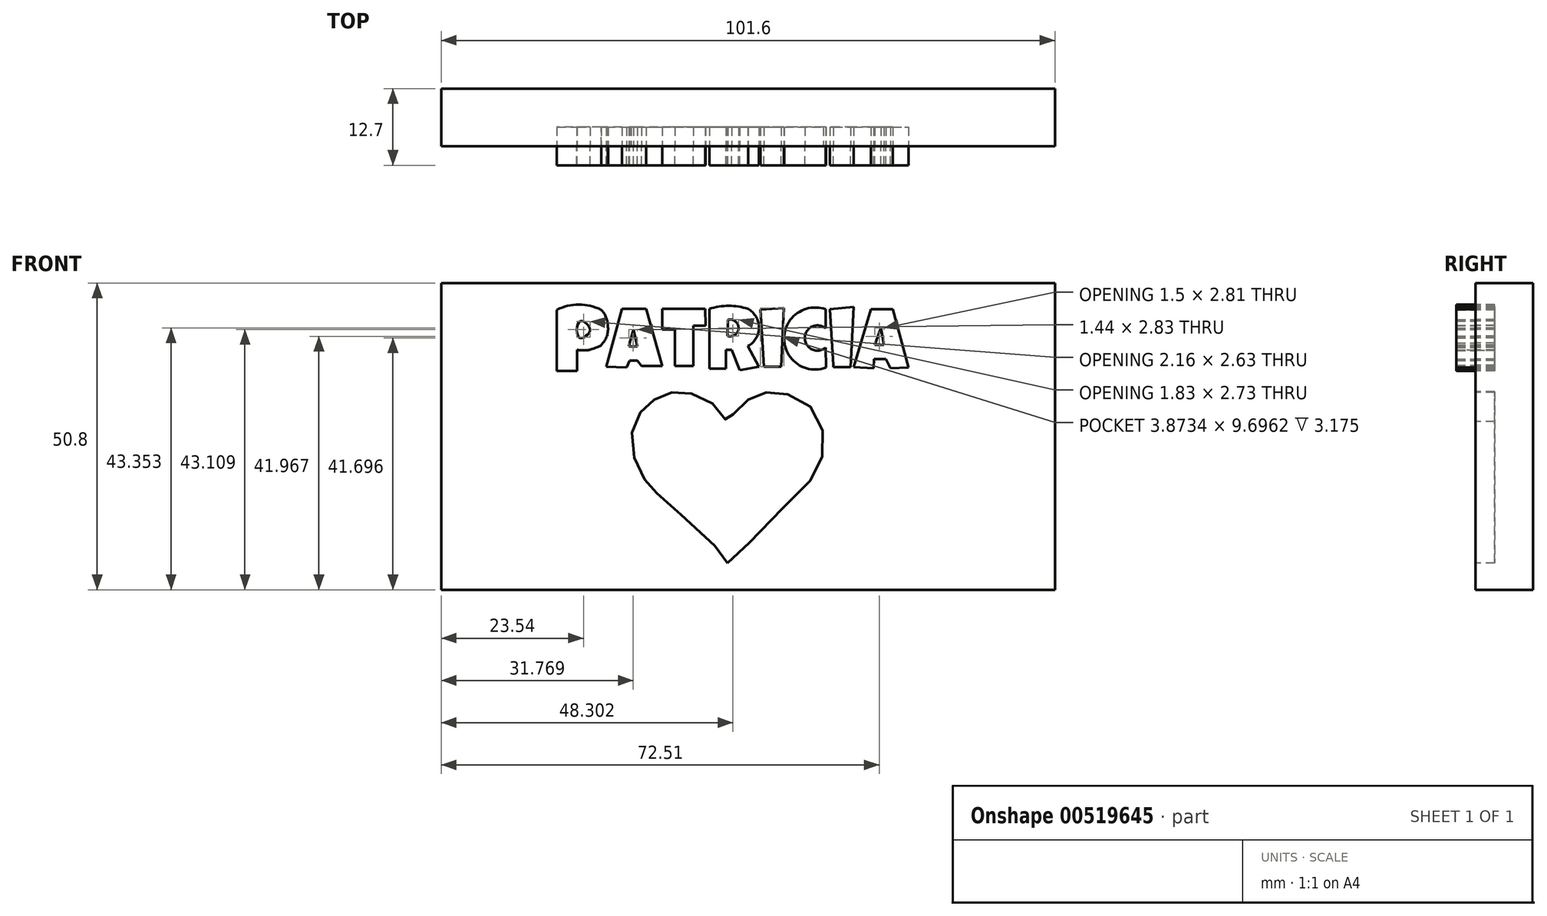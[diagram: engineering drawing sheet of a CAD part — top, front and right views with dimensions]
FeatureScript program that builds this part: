
annotation { "Feature Type Name" : "Feature", "Feature Type Description" : "" }
export const myFeature = defineFeature(function(context is Context, id is Id, definition is map)
    precondition{}
    {
        {
            var Q0;
            Q0=qCreatedBy(makeId("Front.planeOp"),FACE);
            var Q1;
            Q1=qCreatedBy(makeId("Front.planeOp"),FACE);
            var Q2;
            Q2=qCreatedBy(makeId("Front.planeOp"),FACE);
            var Q3;
            Q3=qCreatedBy(makeId("Front.planeOp"),FACE);
            var sketch = newSketch(context, id + "F0", { "sketchPlane" : qUnion([Q0, Q1, Q2, Q3])});
            skLineSegment(sketch, "E0.bottom", {"start": v(-89.5, 39.79) * mm, "end": v(12.1, 39.79) * mm});
            skLineSegment(sketch, "E0.top", {"start": v(-89.5, -11.01) * mm, "end": v(12.1, -11.01) * mm});
            skLineSegment(sketch, "E0.left", {"start": v(-89.5, 39.79) * mm, "end": v(-89.5, -11.01) * mm});
            skLineSegment(sketch, "E0.right", {"start": v(12.1, 39.79) * mm, "end": v(12.1, -11.01) * mm});
            skSolve(sketch);
        }
        {
            var Q0;
            Q0=makeQuery(id+"F0.imprint","IMPRINT",FACE,{"disambiguationData":[TD([[makeQuery(id+"F0.imprint","IMPRINT",EDGE,{"derivedFrom":sQuery(id+"F0.wireOp",EDGE,"E0.bottom")}),-1.0]])]});
            extrude(context, id + "F1", {"entities" : qUnion([Q0]), "depth" : 9.52 * mm, "offsetDistance" : 25.4 * mm});
        }
        {
            var Q0;
            Q0=makeQuery(id+"F1.opExtrude","CAP_FACE",FACE,{"disambiguationData":[OSD([sQuery(id+"F0.wireOp",EDGE,"E0.bottom"),sQuery(id+"F0.wireOp",EDGE,"E0.top"),sQuery(id+"F0.wireOp",EDGE,"E0.left"),sQuery(id+"F0.wireOp",EDGE,"E0.right")])],"isStart":false});
            var sketch = newSketch(context, id + "F2", { "sketchPlane" : qUnion([Q0])});
            skLineSegment(sketch, "E1", {"start": v(-70.4, 35.35) * mm, "end": v(-70.4, 25.24) * mm});
            skLineSegment(sketch, "E2", {"start": v(-70.4, 25.24) * mm, "end": v(-66.98, 25.24) * mm});
            skLineSegment(sketch, "E3", {"start": v(-66.98, 25.24) * mm, "end": v(-66.98, 28.77) * mm});
            skArc(sketch, "E4", {"start": v(-63.03, 35.35) * mm, "mid": v(-66.71, 36.2) * mm, "end": v(-70.4, 35.35) * mm});
            skArc(sketch, "E5", {"start": v(-61.93, 32.72) * mm, "mid": v(-62.22, 34.15) * mm, "end": v(-63.03, 35.35) * mm});
            skArc(sketch, "E6", {"start": v(-63.03, 29.54) * mm, "mid": v(-62.08, 31) * mm, "end": v(-61.93, 32.72) * mm});
            skFitSpline(sketch, "E7", {"points": [v(-63.03, 29.54) * mm, v(-64.56, 28.84) * mm, v(-65.66, 28.64) * mm, v(-66.98, 28.77) * mm, v(-63.03, 29.54) * mm]});
            skFitSpline(sketch, "E8", {"points": [v(-58.8, 25.8) * mm, v(-58.32, 26.97) * mm], "startDerivative": vector(0.48, 1.18) * mm, "endDerivative": vector(0.48, 1.18) * mm});
            skFitSpline(sketch, "E9", {"points": [v(-58.32, 26.97) * mm, v(-57, 26.97) * mm], "startDerivative": vector(1.32, 0) * mm, "endDerivative": vector(1.32, 0) * mm});
            skLineSegment(sketch, "E10", {"start": v(-59.57, 35.5) * mm, "end": v(-62.2, 25.93) * mm});
            skLineSegment(sketch, "E11", {"start": v(-62.2, 25.93) * mm, "end": v(-58.8, 25.8) * mm});
            skLineSegment(sketch, "E12", {"start": v(-57.89, 26.97) * mm, "end": v(-57, 26.97) * mm});
            skLineSegment(sketch, "E13", {"start": v(-59.57, 35.5) * mm, "end": v(-55.55, 35.5) * mm});
            skLineSegment(sketch, "E14", {"start": v(-55.55, 35.5) * mm, "end": v(-52.92, 26.06) * mm});
            skLineSegment(sketch, "E15", {"start": v(-57.7, 32.1) * mm, "end": v(-58.32, 29.83) * mm});
            skLineSegment(sketch, "E16", {"start": v(-57, 29.27) * mm, "end": v(-57.7, 32.1) * mm});
            skLineSegment(sketch, "E17", {"start": v(-52.92, 35.5) * mm, "end": v(-52.92, 32.1) * mm});
            skLineSegment(sketch, "E18", {"start": v(-52.92, 32.1) * mm, "end": v(-50.84, 32.1) * mm});
            skLineSegment(sketch, "E19", {"start": v(-50.84, 32.1) * mm, "end": v(-50.84, 26.06) * mm});
            skLineSegment(sketch, "E20", {"start": v(-50.84, 26.06) * mm, "end": v(-47.8, 26.06) * mm});
            skLineSegment(sketch, "E21", {"start": v(-47.8, 26.06) * mm, "end": v(-47.8, 32.72) * mm});
            skLineSegment(sketch, "E22", {"start": v(-45.1, 32.25) * mm, "end": v(-45.1, 35.5) * mm});
            skPoint(sketch, "E23.end.orphan", {"position": v(-56.31, 26.06) * mm});
            skLineSegment(sketch, "E24", {"start": v(-47.8, 32.72) * mm, "end": v(-45.74, 32.72) * mm});
            skLineSegment(sketch, "E25", {"start": v(-45.1, 32.72) * mm, "end": v(-45.1, 32.72) * mm});
            skLineSegment(sketch, "E26", {"start": v(-45.1, 25.59) * mm, "end": v(-42.4, 25.59) * mm});
            skLineSegment(sketch, "E27", {"start": v(-42.4, 25.59) * mm, "end": v(-42.4, 28.7) * mm});
            skLineSegment(sketch, "E28", {"start": v(-42.4, 28.7) * mm, "end": v(-41.43, 28.7) * mm});
            skLineSegment(sketch, "E29", {"start": v(-41.43, 28.7) * mm, "end": v(-40.1, 25.38) * mm});
            skLineSegment(sketch, "E30", {"start": v(-40.1, 25.38) * mm, "end": v(-36.92, 25.93) * mm});
            skLineSegment(sketch, "E31", {"start": v(-36.92, 25.93) * mm, "end": v(-38.72, 29.33) * mm});
            skLineSegment(sketch, "E32", {"start": v(-36.65, 35.5) * mm, "end": v(-36.1, 25.93) * mm});
            skLineSegment(sketch, "E33", {"start": v(-36.1, 25.93) * mm, "end": v(-33.25, 25.93) * mm});
            skLineSegment(sketch, "E34", {"start": v(-33.25, 25.93) * mm, "end": v(-32.77, 35.63) * mm});
            skLineSegment(sketch, "E35", {"start": v(-32.77, 35.63) * mm, "end": v(-36.64, 35.4) * mm});
            skLineSegment(sketch, "E36", {"start": v(-25.84, 35.42) * mm, "end": v(-25.84, 32.25) * mm});
            skLineSegment(sketch, "E37", {"start": v(-25.15, 35.42) * mm, "end": v(-24.6, 26.21) * mm});
            skLineSegment(sketch, "E38", {"start": v(-24.6, 26.21) * mm, "end": v(-24.6, 25.86) * mm});
            skLineSegment(sketch, "E39", {"start": v(-24.6, 25.86) * mm, "end": v(-21.76, 25.86) * mm});
            skLineSegment(sketch, "E40", {"start": v(-21.76, 25.86) * mm, "end": v(-21.2, 35.84) * mm});
            skLineSegment(sketch, "E41", {"start": v(-21.2, 35.84) * mm, "end": v(-25.15, 35.42) * mm});
            skLineSegment(sketch, "E42", {"start": v(-21.25, 25.84) * mm, "end": v(-17.92, 25.65) * mm});
            skLineSegment(sketch, "E43", {"start": v(-17.92, 25.65) * mm, "end": v(-17.84, 27.2) * mm});
            skLineSegment(sketch, "E44", {"start": v(-17.84, 27.2) * mm, "end": v(-15.87, 27.2) * mm});
            skLineSegment(sketch, "E45", {"start": v(-15.87, 27.2) * mm, "end": v(-15.1, 25.65) * mm});
            skLineSegment(sketch, "E46", {"start": v(-15.1, 25.65) * mm, "end": v(-12.16, 25.83) * mm});
            skLineSegment(sketch, "E47", {"start": v(-14.76, 35.42) * mm, "end": v(-18.36, 35.42) * mm});
            skPoint(sketch, "E48.end.orphan", {"position": v(-25.84, 26.21) * mm});
            skPoint(sketch, "E48.start.orphan", {"position": v(-25.84, 29.12) * mm});
            skLineSegment(sketch, "E49", {"start": v(-25.8, 25.78) * mm, "end": v(-25.84, 29.12) * mm});
            skPoint(sketch, "E50.0.internal.snap0", {"position": v(-66.71, 36.2) * mm});
            skPoint(sketch, "E50.1.internal.snap0", {"position": v(-66.71, 36.2) * mm});
            skFitSpline(sketch, "E50", {"points": [v(-66.71, 33.3) * mm, v(-66.71, 30.8) * mm, v(-65.31, 31.22) * mm, v(-64.89, 32.17) * mm, v(-65.66, 33.24) * mm, v(-66.71, 33.3) * mm]});
            skArc(sketch, "E51", {"start": v(-25.84, 32.25) * mm, "mid": v(-29.3, 30.68) * mm, "end": v(-25.84, 29.12) * mm});
            skArc(sketch, "E52", {"start": v(-25.84, 35.42) * mm, "mid": v(-32.75, 30.57) * mm, "end": v(-25.8, 25.78) * mm});
            skArc(sketch, "E53", {"start": v(-42.11, 31.04) * mm, "mid": v(-40.28, 32.3) * mm, "end": v(-42.03, 33.69) * mm});
            skLineSegment(sketch, "E54", {"start": v(-42.03, 33.69) * mm, "end": v(-42.11, 31.04) * mm});
            skArc(sketch, "E55", {"start": v(-38.71, 35.5) * mm, "mid": v(-41.9, 36) * mm, "end": v(-45.1, 35.5) * mm});
            skArc(sketch, "E56", {"start": v(-38.72, 29.33) * mm, "mid": v(-36.9, 32.4) * mm, "end": v(-38.71, 35.5) * mm});
            skLineSegment(sketch, "E57", {"start": v(-16.74, 32.36) * mm, "end": v(-17.74, 29.55) * mm});
            skLineSegment(sketch, "E58", {"start": v(-17.74, 29.55) * mm, "end": v(-16.24, 29.55) * mm});
            skLineSegment(sketch, "E59", {"start": v(-16.24, 29.55) * mm, "end": v(-16.74, 32.36) * mm});
            skLineSegment(sketch, "E60", {"start": v(-57, 26.97) * mm, "end": v(-56.31, 26.06) * mm});
            skLineSegment(sketch, "E61", {"start": v(-56.31, 26.06) * mm, "end": v(-52.92, 26.06) * mm});
            skLineSegment(sketch, "E62", {"start": v(-25.84, 29.12) * mm, "end": v(-25.8, 25.78) * mm});
            skPoint(sketch, "E63.orphan", {"position": v(-25.84, 32.38) * mm});
            skLineSegment(sketch, "E64", {"start": v(-18.36, 35.42) * mm, "end": v(-21.25, 25.84) * mm});
            skLineSegment(sketch, "E65", {"start": v(-14.76, 35.42) * mm, "end": v(-12.16, 25.83) * mm});
            skPoint(sketch, "E66.orphan", {"position": v(-11.57, 25.86) * mm});
            skLineSegment(sketch, "E67", {"start": v(-57, 29.27) * mm, "end": v(-58.45, 29.27) * mm});
            skLineSegment(sketch, "E68", {"start": v(-58.45, 29.27) * mm, "end": v(-58.32, 29.83) * mm});
            skLineSegment(sketch, "E69", {"start": v(-45.1, 35.5) * mm, "end": v(-45.1, 35.5) * mm});
            skLineSegment(sketch, "E70", {"start": v(-45.1, 32.72) * mm, "end": v(-45.1, 25.59) * mm});
            skLineSegment(sketch, "E71", {"start": v(-45.8, 35.5) * mm, "end": v(-52.92, 35.5) * mm});
            skLineSegment(sketch, "E72", {"start": v(-45.8, 35.5) * mm, "end": v(-45.74, 32.72) * mm});
            skSolve(sketch);
        }
        {
            var Q0;
            Q0=makeQuery(id+"F2.imprint","IMPRINT",FACE,{"disambiguationData":[TD([[makeQuery(id+"F2.imprint","IMPRINT",EDGE,{"derivedFrom":sQuery(id+"F2.wireOp",EDGE,"E1")}),-1.0]])]});
            var sketch = newSketch(context, id + "F3", { "sketchPlane" : qUnion([Q0])});
            skFitSpline(sketch, "E73", {"points": [v(-42.1, -6.57) * mm, v(-43.08, -5.2) * mm, v(-52.17, 3.49) * mm, v(-54.64, 5.84) * mm, v(-56.38, 8.17) * mm, v(-57.94, 12.5) * mm, v(-57.53, 16.5) * mm, v(-55.85, 19.13) * mm, v(-54, 20.57) * mm, v(-51.59, 21.6) * mm, v(-49.13, 21.7) * mm, v(-45.45, 20.47) * mm, v(-43.03, 18.1) * mm, v(-42.1, 16.84) * mm, v(-41.56, 17.55) * mm, v(-39.77, 19.62) * mm, v(-37.15, 21.3) * mm, v(-34.64, 21.7) * mm, v(-30.85, 20.92) * mm, v(-27.08, 17.6) * mm, v(-26.3, 12.62) * mm, v(-27.5, 8.23) * mm, v(-35.54, 0) * mm, v(-42.1, -6.57) * mm]});
            skFitSpline(sketch, "E74", {"points": [v(109.36, 3.64) * mm, v(120.38, -22.61) * mm], "startDerivative": vector(11.02, -26.25) * mm, "endDerivative": vector(11.02, -26.25) * mm});
            skSolve(sketch);
        }
        {
            var Q0;
            Q0 = qSketchRegion(id + "F3", true);
            var Q1;
            Q1 = qSketchRegion(id + "F2", true);
            extrude(context, id + "F4", {"entities" : qUnion([Q0, Q1]), "operationType" : NewBodyOperationType.REMOVE, "oppositeDirection" : true, "depth" : 3.17 * mm, "offsetDistance" : 25.4 * mm});
        }
        {
            var Q0;
            Q0 = qSketchRegion(id + "F2", true);
            extrude(context, id + "F5", {"entities" : qUnion([Q0]), "depth" : 3.17 * mm, "offsetDistance" : 25.4 * mm});
        }
    });
